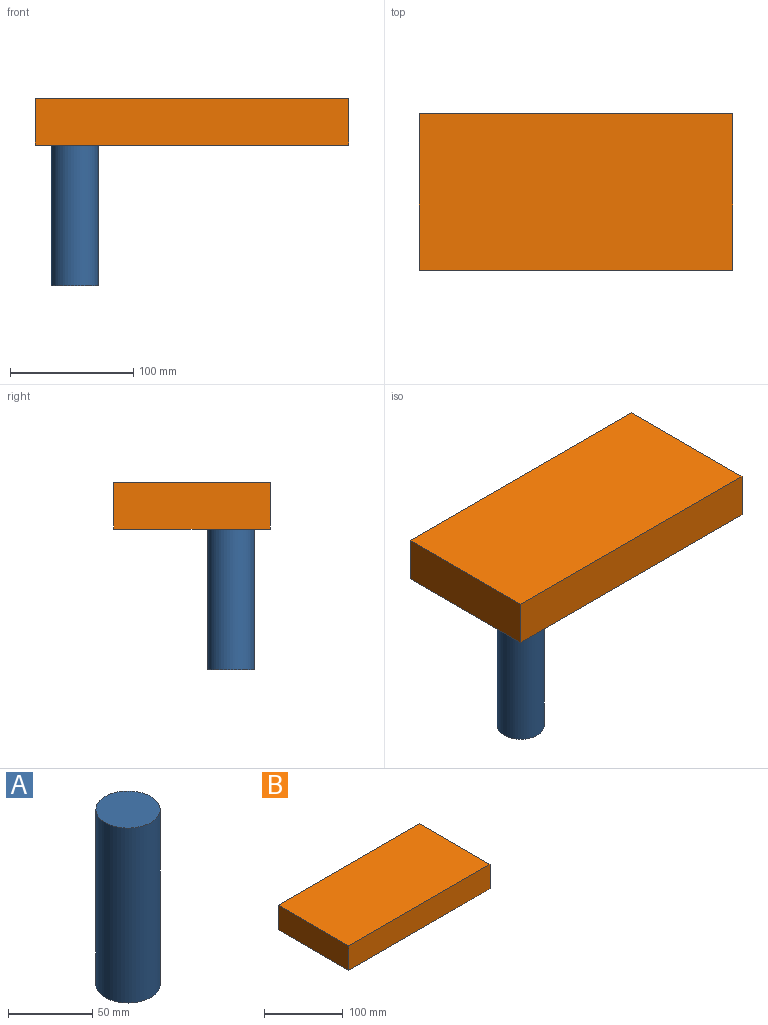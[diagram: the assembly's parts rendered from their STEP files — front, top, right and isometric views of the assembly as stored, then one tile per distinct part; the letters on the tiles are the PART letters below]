
ASSEMBLY  parts=2 mates=1
PART A: 3 faces, bbox 38.1x38.1x127 mm
  f0: cylinder r=19.05mm len=127mm, axis (0,0,-1), area 15201.2mm2, adj f1,f2
  f1: plane 38.1x38.1mm, normal (0,0,1), area 1140.1mm2, adj f0
  f2: plane 38.1x38.1mm, normal (0,0,-1), area 1140.1mm2, adj f0
PART B: 8 faces, bbox 254x127x38.1 mm
  f0: plane 254x38.1mm, normal (0,-1,0), area 9677.4mm2, adj f1,f3,f4,f5
  f1: plane 127x38.1mm, normal (1,0,0), area 4838.7mm2, adj f0,f2,f4,f5
  f2: plane 254x38.1mm, normal (0,1,0), area 9677.4mm2, adj f1,f3,f4,f5
  f3: plane 127x38.1mm, normal (-1,0,0), area 4838.7mm2, adj f0,f2,f4,f5
  f4: plane 254x127mm, normal (0,0,1), area 32258mm2, adj f0,f1,f2,f3
  f5: plane 254x127mm, normal (0,0,-1), area 31117.9mm2, adj f0,f1,f2,f3,f6
  f6: cylinder r=19.05mm len=38.1mm, axis (0,0,-1), area 1520.1mm2, adj f5,f7
  f7: plane 38.1x38.1mm, normal (0,0,-1), area 1140.1mm2, adj f6
PLACE A t=(107.44,10.3,-114.3)mm
PLACE B at identity
MATE fastened A.f0 <-> B.f6  axis (0,0,1) through (-95.25,-31.75,12.7)mm
